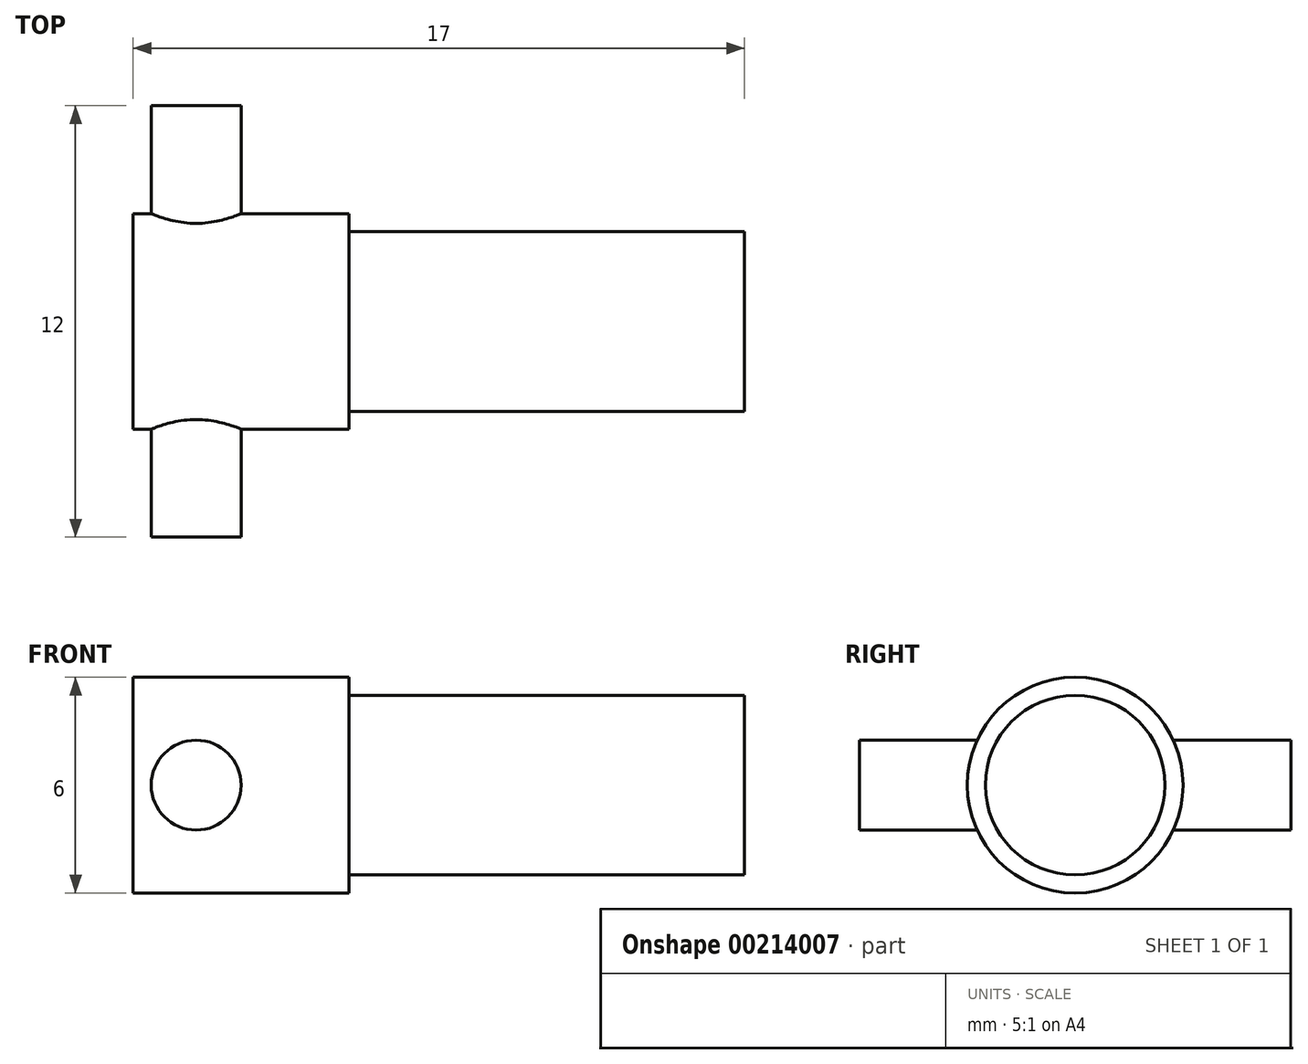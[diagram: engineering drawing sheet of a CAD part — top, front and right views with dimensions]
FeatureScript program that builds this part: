
annotation { "Feature Type Name" : "Feature", "Feature Type Description" : "" }
export const myFeature = defineFeature(function(context is Context, id is Id, definition is map)
    precondition{}
    {
        {
            var Q0;
            Q0=qCreatedBy(makeId("Right.planeOp"),FACE);
            var sketch = newSketch(context, id + "F0", { "sketchPlane" : qUnion([Q0])});
            skCircle(sketch, "E0", {"center": v(0, 0) * mm, "radius": 3 * mm});
            skSolve(sketch);
        }
        {
            var Q0;
            Q0 = qSketchRegion(id + "F0", true);
            extrude(context, id + "F1", {"entities" : qUnion([Q0]), "depth" : 6 * mm});
        }
        {
            var Q0;
            Q0=makeQuery(id+"F1.opExtrude","CAP_FACE",FACE,{"disambiguationData":[OSD([sQuery(id+"F0.wireOp",EDGE,"E0")])],"isStart":false});
            var sketch = newSketch(context, id + "F2", { "sketchPlane" : qUnion([Q0])});
            skCircle(sketch, "E1", {"center": v(0, 0) * mm, "radius": 2.5 * mm});
            skSolve(sketch);
        }
        {
            var Q0;
            Q0 = qSketchRegion(id + "F2", true);
            extrude(context, id + "F3", {"entities" : qUnion([Q0]), "operationType" : NewBodyOperationType.ADD, "depth" : 11 * mm});
        }
        {
            var Q0;
            Q0=qCreatedBy(makeId("Front.planeOp"),FACE);
            var sketch = newSketch(context, id + "F4", { "sketchPlane" : qUnion([Q0])});
            skLineSegment(sketch, "E2", {"start": v(0, 0) * mm, "end": v(20.26, 0) * mm, "construction": true});
            skCircle(sketch, "E3", {"center": v(1.75, 0) * mm, "radius": 1.25 * mm});
            skSolve(sketch);
        }
        {
            var Q0;
            Q0 = qSketchRegion(id + "F4", true);
            extrude(context, id + "F5", {"entities" : qUnion([Q0]), "operationType" : NewBodyOperationType.ADD, "endBound" : BoundingType.SYMMETRIC, "depth" : 12 * mm});
        }
    });
